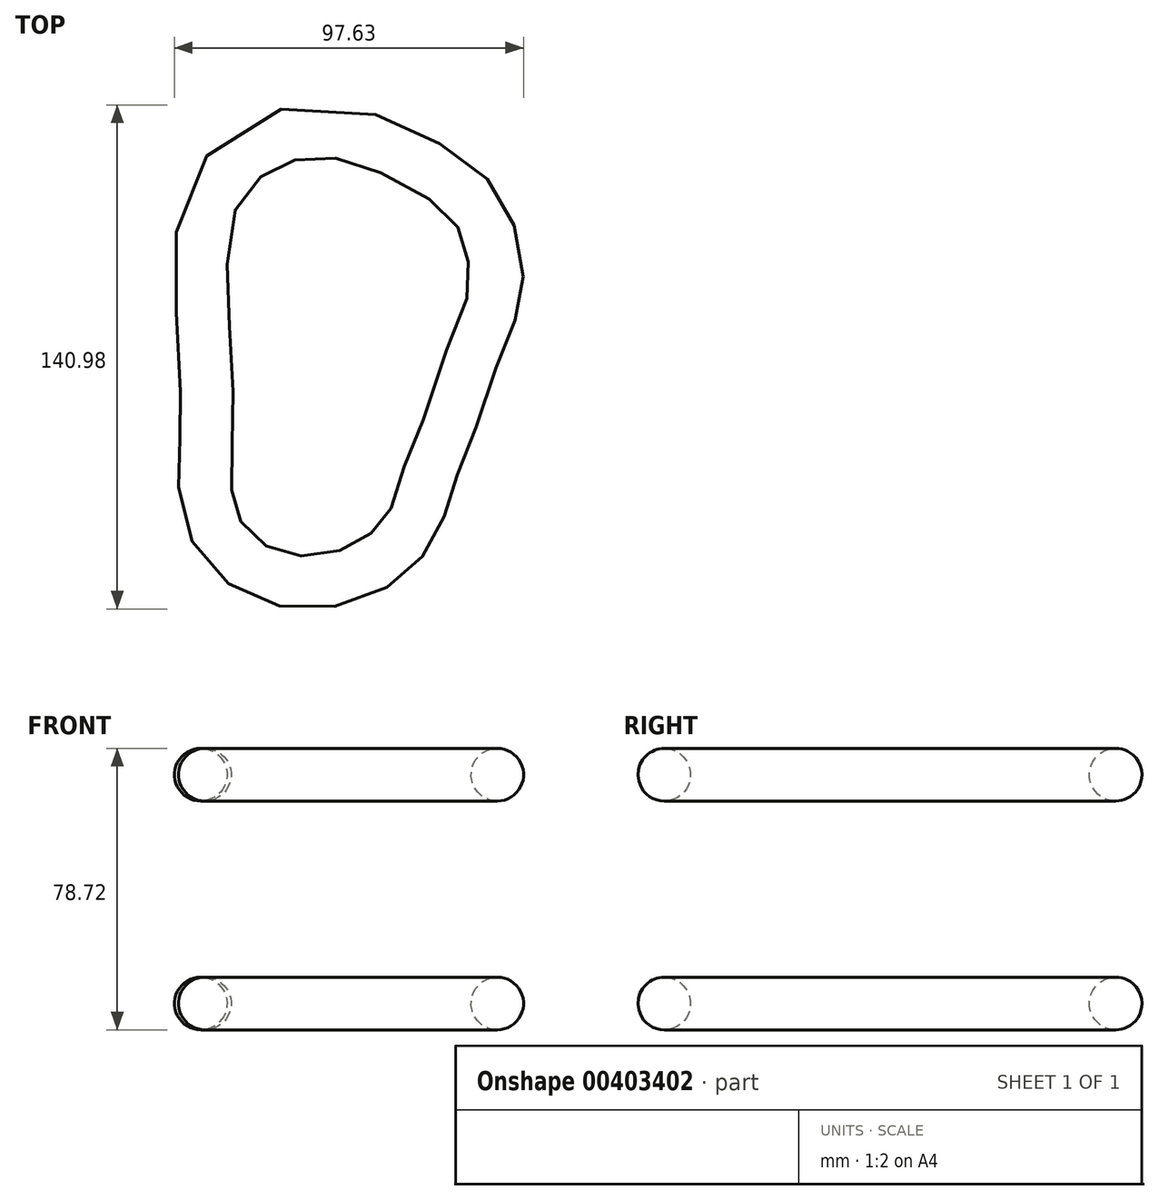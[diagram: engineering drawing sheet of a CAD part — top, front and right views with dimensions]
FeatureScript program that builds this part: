
annotation { "Feature Type Name" : "Feature", "Feature Type Description" : "" }
export const myFeature = defineFeature(function(context is Context, id is Id, definition is map)
    precondition{}
    {
        {
            var Q0;
            Q0=qCreatedBy(makeId("Top.planeOp"),FACE);
            var sketch = newSketch(context, id + "F0", { "sketchPlane" : qUnion([Q0])});
            skFitSpline(sketch, "E0", {"points": [v(-27.55, 63.05) * mm, v(-33.23, 55.93) * mm, v(-36.95, 40.91) * mm, v(-36.76, 26.23) * mm, v(-36.12, 9.54) * mm, v(-35.31, -3.46) * mm, v(-35.67, -14.8) * mm, v(-35.94, -22.36) * mm, v(-35.85, -28.22) * mm, v(-34.59, -34.34) * mm, v(-31.8, -40.38) * mm, v(-26.48, -45.96) * mm, v(-20.9, -49.57) * mm, v(-12.88, -51.82) * mm, v(-4.14, -51.82) * mm, v(4.24, -49.57) * mm, v(10.18, -46.68) * mm, v(15.86, -41.64) * mm, v(19.01, -37.77) * mm, v(21, -33.35) * mm, v(21.62, -31.73) * mm, v(25.23, -20.1) * mm, v(26.94, -16.87) * mm, v(31.26, -4.62) * mm, v(38.1, 15.2) * mm, v(41.8, 24.03) * mm, v(43.15, 29.08) * mm, v(42.97, 33.04) * mm, v(41.53, 42.05) * mm, v(39.19, 48.17) * mm, v(35.23, 53.76) * mm, v(27.2, 59.98) * mm, v(16.3, 65.92) * mm, v(7.3, 69.43) * mm, v(-1.08, 71.42) * mm, v(-10.18, 71.15) * mm, v(-16.3, 69.88) * mm, v(-22.52, 66.73) * mm, v(-27.55, 63.05) * mm]});
            skFitSpline(sketch, "E1", {"points": [v(11.8, 53.67) * mm, v(3.79, 56.91) * mm, v(-1.53, 58.53) * mm, v(-6.21, 58.71) * mm, v(-10.54, 58.08) * mm, v(-15.85, 55.11) * mm, v(-20.54, 50.43) * mm, v(-22.25, 46.82) * mm, v(-23.33, 42.68) * mm, v(-23.06, 36.37) * mm, v(-23.06, 25.56) * mm, v(-22.43, 15.74) * mm, v(-22.16, 7.28) * mm, v(-21.89, 0) * mm, v(-21.53, -5.97) * mm, v(-21.8, -16.96) * mm, v(-22.34, -21.91) * mm, v(-22.52, -25.6) * mm, v(-22.43, -28.04) * mm, v(-21.26, -31) * mm, v(-19.37, -34.07) * mm, v(-17.02, -36.69) * mm, v(-14.41, -38.3) * mm, v(-11.35, -39.39) * mm, v(-6.75, -39.2) * mm, v(-1.26, -38.13) * mm, v(2.89, -36.5) * mm, v(6.04, -33.98) * mm, v(6.49, -32.1) * mm, v(7.84, -31.28) * mm, v(10.27, -25.15) * mm, v(11.8, -20.65) * mm, v(13.15, -17.05) * mm, v(14.06, -14.8) * mm, v(14.06, -13.44) * mm, v(15.68, -9.39) * mm, v(21.62, 7.9) * mm, v(25.77, 19.35) * mm, v(26.22, 20.79) * mm, v(27.84, 26.2) * mm, v(28.92, 27.45) * mm, v(29.19, 29.53) * mm, v(30, 32.95) * mm, v(29.28, 39.89) * mm, v(26.76, 44.57) * mm, v(22.25, 48.08) * mm, v(11.8, 53.67) * mm]});
            skSolve(sketch);
        }
        {
            var Q0;
            Q0=qCreatedBy(makeId("Front.planeOp"),FACE);
            var sketch = newSketch(context, id + "F1", { "sketchPlane" : qUnion([Q0])});
            skCircle(sketch, "E2", {"center": v(-36.74, 0) * mm, "radius": 7.36 * mm});
            skSolve(sketch);
        }
        {
            var Q0;
            Q0=makeQuery(id+"F1.imprint","IMPRINT",FACE,{"disambiguationData":[TD([[makeQuery(id+"F1.imprint","IMPRINT",EDGE,{"derivedFrom":sQuery(id+"F1.wireOp",EDGE,"E2")}),1.0]])]});
            var Q1;
            Q1=sQuery(id+"F0.wireOp",EDGE,"E0");
            sweep(context, id + "F2", {"profiles" : qUnion([Q0]), "path" : qUnion([Q1])});
        }
        {
            var Q0;
            Q0=makeQuery(id+"F2.opSweep","SWEPT_BODY",BODY,{"disambiguationData":[OSD([sQuery(id+"F0.wireOp",EDGE,"E0"),sQuery(id+"F1.wireOp",EDGE,"E2")])]});
            transform(context, id + "F3", {"entities" : qUnion([Q0]), "transformType" : TransformType.TRANSLATION_3D, "dx" : 0 * mm, "dy" : 0 * mm, "dz" : -64 * mm, "makeCopy" : true});
        }
    });
